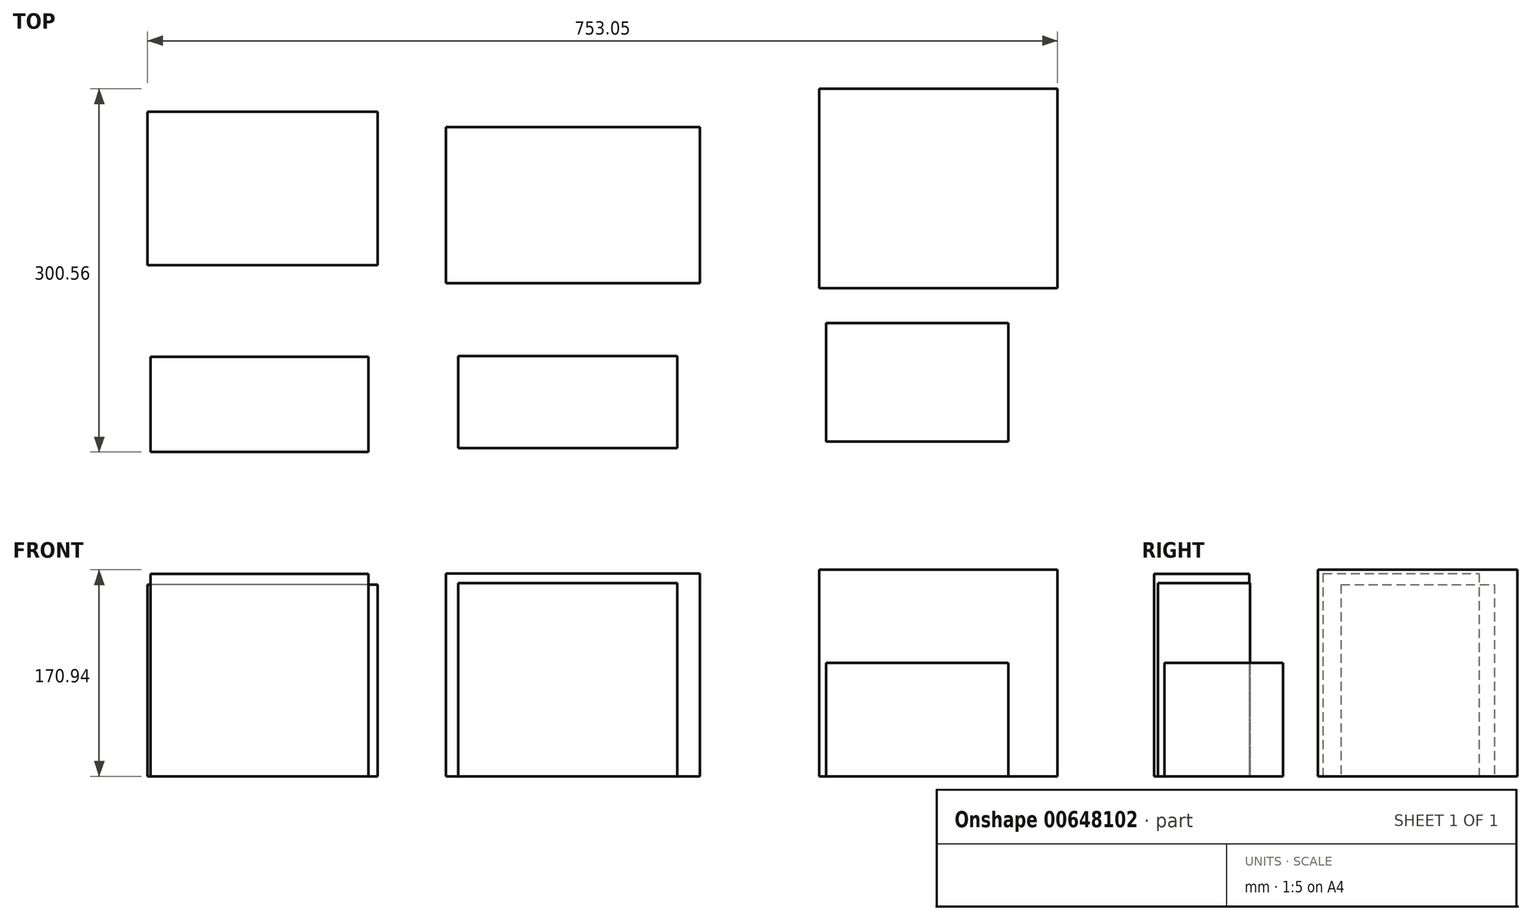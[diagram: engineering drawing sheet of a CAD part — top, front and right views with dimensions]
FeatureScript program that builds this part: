
annotation { "Feature Type Name" : "Feature", "Feature Type Description" : "" }
export const myFeature = defineFeature(function(context is Context, id is Id, definition is map)
    precondition{}
    {
        {
            var Q0;
            Q0=qCreatedBy(makeId("Top.planeOp"),FACE);
            var sketch = newSketch(context, id + "F0", { "sketchPlane" : qUnion([Q0])});
            skLineSegment(sketch, "E0.bottom", {"start": v(98.55, -82.55) * mm, "end": v(-98.55, -82.55) * mm});
            skLineSegment(sketch, "E0.top", {"start": v(98.55, 82.55) * mm, "end": v(-98.55, 82.55) * mm});
            skLineSegment(sketch, "E0.left", {"start": v(98.55, -82.55) * mm, "end": v(98.55, 82.55) * mm});
            skLineSegment(sketch, "E0.right", {"start": v(-98.55, -82.55) * mm, "end": v(-98.55, 82.55) * mm});
            skPoint(sketch, "E0.middle", {"position": v(0, 0) * mm});
            skSolve(sketch);
        }
        {
            var Q0;
            Q0 = qSketchRegion(id + "F0", true);
            extrude(context, id + "F1", {"entities" : qUnion([Q0]), "depth" : 170.94 * mm, "offsetDistance" : 25.4 * mm});
        }
        {
            var Q0;
            Q0=qCreatedBy(makeId("Top.planeOp"),FACE);
            var sketch = newSketch(context, id + "F2", { "sketchPlane" : qUnion([Q0])});
            skLineSegment(sketch, "E1.bottom", {"start": v(-197.38, -78.23) * mm, "end": v(-407.44, -78.23) * mm});
            skLineSegment(sketch, "E1.top", {"start": v(-197.38, 50.8) * mm, "end": v(-407.44, 50.8) * mm});
            skLineSegment(sketch, "E1.left", {"start": v(-197.38, -78.23) * mm, "end": v(-197.38, 50.8) * mm});
            skLineSegment(sketch, "E1.right", {"start": v(-407.44, -78.23) * mm, "end": v(-407.44, 50.8) * mm});
            skPoint(sketch, "E1.middle", {"position": v(-302.4, -13.72) * mm});
            skSolve(sketch);
        }
        {
            var Q0;
            Q0 = qSketchRegion(id + "F2", true);
            extrude(context, id + "F3", {"entities" : qUnion([Q0]), "depth" : 167.9 * mm, "offsetDistance" : 25.4 * mm});
        }
        {
            var Q0;
            Q0=qCreatedBy(makeId("Top.planeOp"),FACE);
            var sketch = newSketch(context, id + "F4", { "sketchPlane" : qUnion([Q0])});
            skLineSegment(sketch, "E2.bottom", {"start": v(-216.23, -214.85) * mm, "end": v(-397.33, -214.85) * mm});
            skLineSegment(sketch, "E2.top", {"start": v(-216.23, -138.65) * mm, "end": v(-397.33, -138.65) * mm});
            skLineSegment(sketch, "E2.left", {"start": v(-216.23, -214.85) * mm, "end": v(-216.23, -138.65) * mm});
            skLineSegment(sketch, "E2.right", {"start": v(-397.33, -214.85) * mm, "end": v(-397.33, -138.65) * mm});
            skPoint(sketch, "E2.middle", {"position": v(-306.78, -176.75) * mm});
            skSolve(sketch);
        }
        {
            var Q0;
            Q0 = qSketchRegion(id + "F4", true);
            extrude(context, id + "F5", {"entities" : qUnion([Q0]), "depth" : 159.77 * mm, "offsetDistance" : 25.4 * mm});
        }
        {
            var Q0;
            Q0=qCreatedBy(makeId("Top.planeOp"),FACE);
            var sketch = newSketch(context, id + "F6", { "sketchPlane" : qUnion([Q0])});
            skLineSegment(sketch, "E3.bottom", {"start": v(57.84, -209.36) * mm, "end": v(-93.04, -209.36) * mm});
            skLineSegment(sketch, "E3.top", {"start": v(57.84, -111.31) * mm, "end": v(-93.04, -111.31) * mm});
            skLineSegment(sketch, "E3.left", {"start": v(57.84, -209.36) * mm, "end": v(57.84, -111.31) * mm});
            skLineSegment(sketch, "E3.right", {"start": v(-93.04, -209.36) * mm, "end": v(-93.04, -111.31) * mm});
            skPoint(sketch, "E3.middle", {"position": v(-17.6, -160.34) * mm});
            skSolve(sketch);
        }
        {
            var Q0;
            Q0 = qSketchRegion(id + "F6", true);
            extrude(context, id + "F7", {"entities" : qUnion([Q0]), "depth" : 93.98 * mm, "offsetDistance" : 25.4 * mm});
        }
        {
            var Q0;
            Q0=qCreatedBy(makeId("Top.planeOp"),FACE);
            var sketch = newSketch(context, id + "F8", { "sketchPlane" : qUnion([Q0])});
            skLineSegment(sketch, "E4.bottom", {"start": v(-464, -63.5) * mm, "end": v(-654.5, -63.5) * mm});
            skLineSegment(sketch, "E4.top", {"start": v(-464, 63.5) * mm, "end": v(-654.5, 63.5) * mm});
            skLineSegment(sketch, "E4.left", {"start": v(-464, -63.5) * mm, "end": v(-464, 63.5) * mm});
            skLineSegment(sketch, "E4.right", {"start": v(-654.5, -63.5) * mm, "end": v(-654.5, 63.5) * mm});
            skPoint(sketch, "E4.middle", {"position": v(-559.25, 0) * mm});
            skSolve(sketch);
        }
        {
            var Q0;
            Q0 = qSketchRegion(id + "F8", true);
            extrude(context, id + "F9", {"entities" : qUnion([Q0]), "depth" : 158.75 * mm, "offsetDistance" : 25.4 * mm});
        }
        {
            var Q0;
            Q0=qCreatedBy(makeId("Top.planeOp"),FACE);
            var sketch = newSketch(context, id + "F10", { "sketchPlane" : qUnion([Q0])});
            skLineSegment(sketch, "E5.bottom", {"start": v(-652.04, -139.27) * mm, "end": v(-471.7, -139.27) * mm});
            skLineSegment(sketch, "E5.top", {"start": v(-652.04, -218) * mm, "end": v(-471.7, -218) * mm});
            skLineSegment(sketch, "E5.left", {"start": v(-652.04, -139.27) * mm, "end": v(-652.04, -218) * mm});
            skLineSegment(sketch, "E5.right", {"start": v(-471.7, -139.27) * mm, "end": v(-471.7, -218) * mm});
            skSolve(sketch);
        }
        {
            var Q0;
            Q0 = qSketchRegion(id + "F10", true);
            extrude(context, id + "F11", {"entities" : qUnion([Q0]), "depth" : 167.64 * mm, "offsetDistance" : 25.4 * mm});
        }
    });
